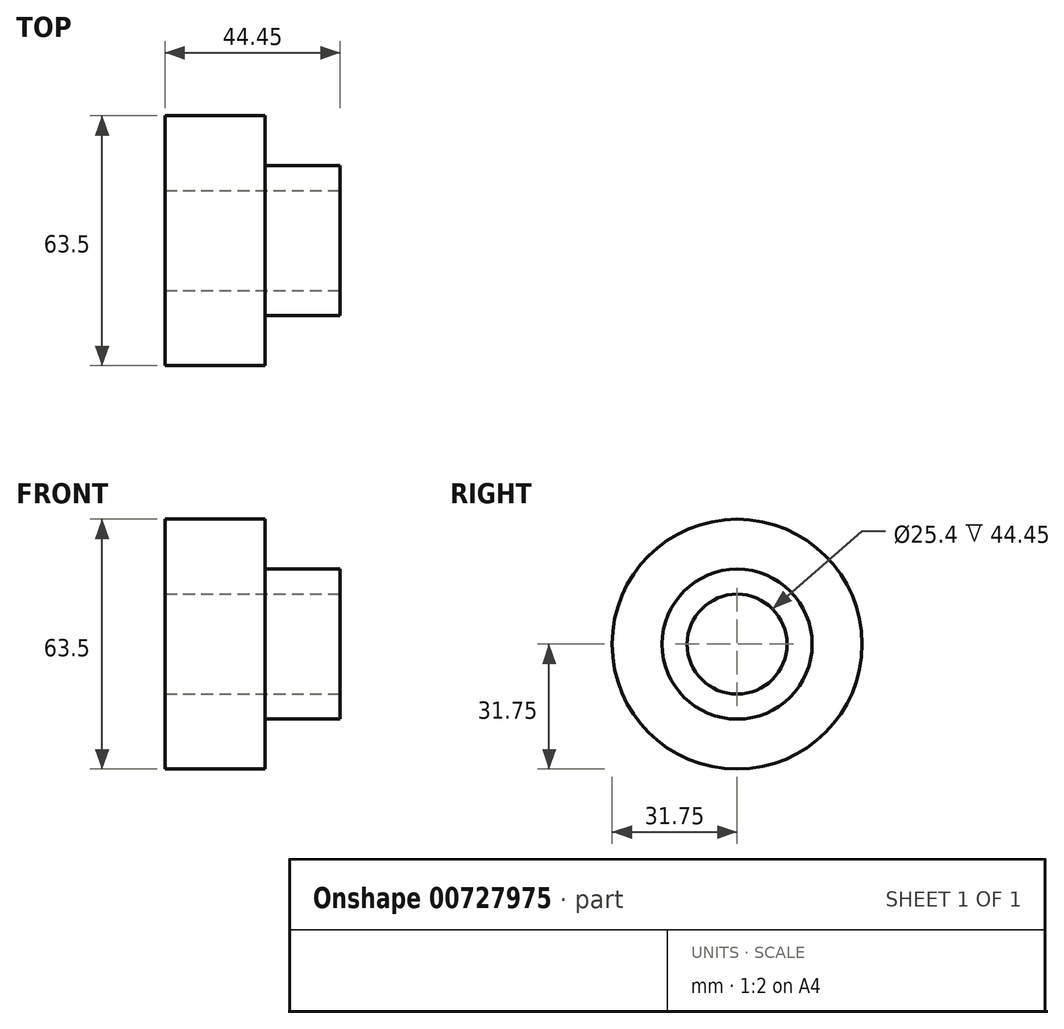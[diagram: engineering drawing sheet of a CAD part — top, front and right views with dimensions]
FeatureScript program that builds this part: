
annotation { "Feature Type Name" : "Feature", "Feature Type Description" : "" }
export const myFeature = defineFeature(function(context is Context, id is Id, definition is map)
    precondition{}
    {
        {
            var Q0;
            Q0=qCreatedBy(makeId("Right.planeOp"),FACE);
            var sketch = newSketch(context, id + "F0", { "sketchPlane" : qUnion([Q0])});
            skCircle(sketch, "E0", {"center": v(0, 0) * mm, "radius": 31.75 * mm});
            skSolve(sketch);
        }
        {
            var Q0;
            Q0=makeQuery(id+"F0.imprint","IMPRINT",FACE,{"disambiguationData":[TD([[makeQuery(id+"F0.imprint","IMPRINT",EDGE,{"derivedFrom":sQuery(id+"F0.wireOp",EDGE,"E0")}),1.0]])]});
            extrude(context, id + "F1", {"entities" : qUnion([Q0]), "depth" : 25.4 * mm, "offsetDistance" : 25.4 * mm});
        }
        {
            var Q0;
            Q0=makeQuery(id+"F1.opExtrude","CAP_FACE",FACE,{"disambiguationData":[OSD([sQuery(id+"F0.wireOp",EDGE,"E0")])],"isStart":false});
            var sketch = newSketch(context, id + "F2", { "sketchPlane" : qUnion([Q0])});
            skCircle(sketch, "E1", {"center": v(0, 0) * mm, "radius": 19.05 * mm});
            skSolve(sketch);
        }
        {
            var Q0;
            Q0=makeQuery(id+"F2.imprint","IMPRINT",FACE,{"disambiguationData":[TD([[makeQuery(id+"F2.imprint","IMPRINT",EDGE,{"derivedFrom":sQuery(id+"F2.wireOp",EDGE,"E1")}),1.0]])]});
            extrude(context, id + "F3", {"entities" : qUnion([Q0]), "operationType" : NewBodyOperationType.ADD, "depth" : 19.05 * mm, "offsetDistance" : 25.4 * mm});
        }
        {
            var Q0;
            Q0=makeQuery(id+"F3.opExtrude","CAP_FACE",FACE,{"disambiguationData":[OSD([sQuery(id+"F2.wireOp",EDGE,"E1")])],"isStart":false});
            var sketch = newSketch(context, id + "F4", { "sketchPlane" : qUnion([Q0])});
            skCircle(sketch, "E2", {"center": v(0, 0) * mm, "radius": 12.7 * mm});
            skSolve(sketch);
        }
        {
            var Q0;
            Q0=makeQuery(id+"F4.imprint","IMPRINT",FACE,{"disambiguationData":[TD([[makeQuery(id+"F4.imprint","IMPRINT",EDGE,{"derivedFrom":sQuery(id+"F4.wireOp",EDGE,"E2")}),1.0]])]});
            extrude(context, id + "F5", {"entities" : qUnion([Q0]), "operationType" : NewBodyOperationType.REMOVE, "oppositeDirection" : true, "depth" : 98.04 * mm, "offsetDistance" : 25.4 * mm});
        }
    });
